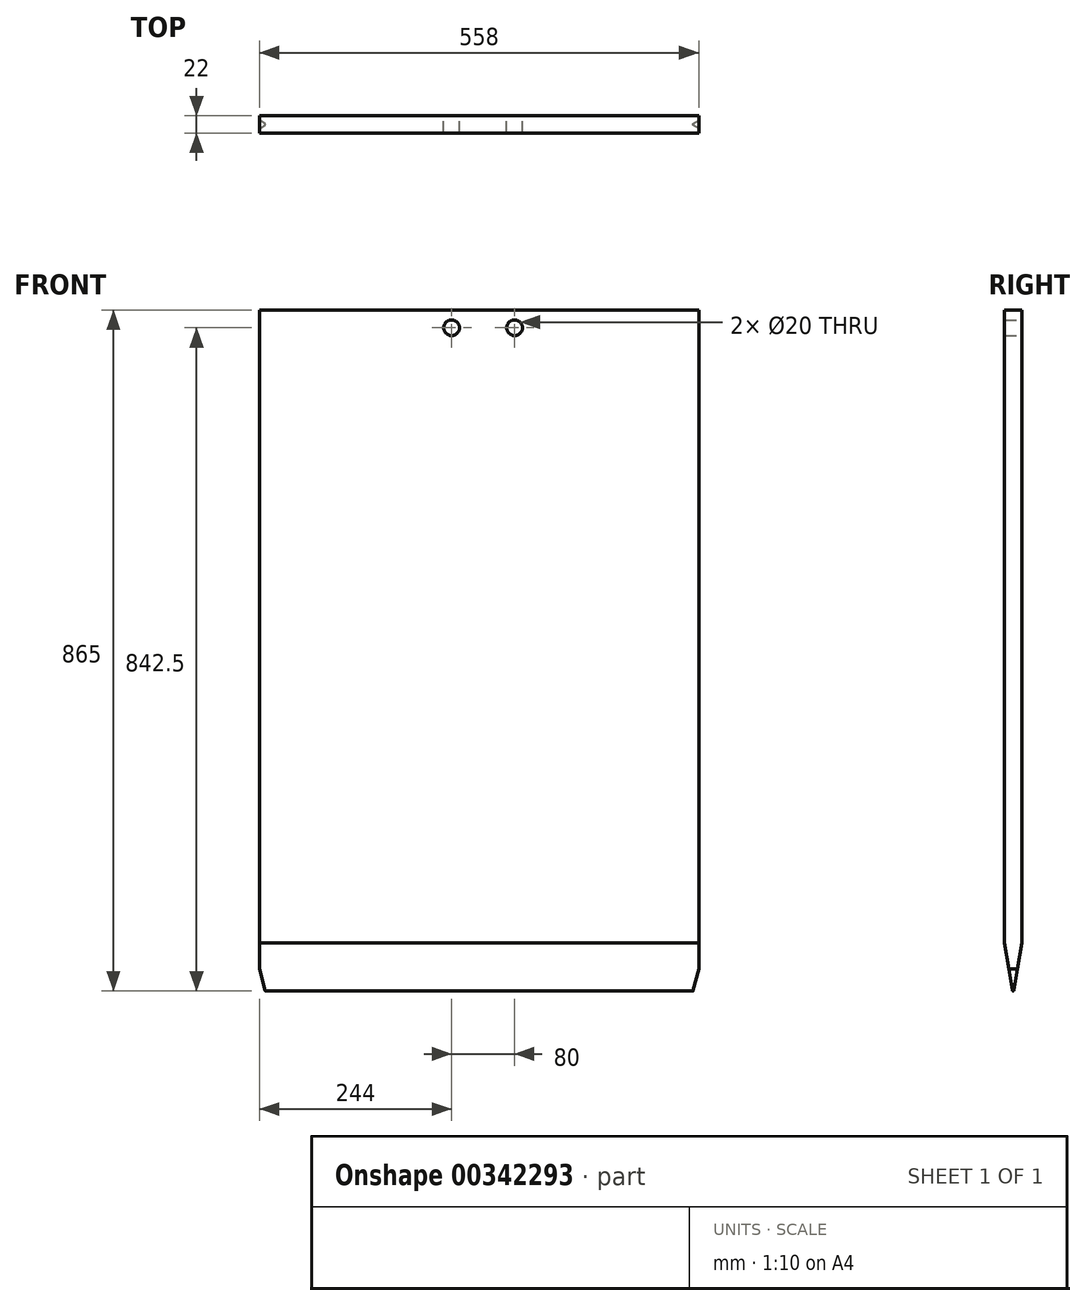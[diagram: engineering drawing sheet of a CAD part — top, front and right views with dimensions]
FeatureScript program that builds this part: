
annotation { "Feature Type Name" : "Feature", "Feature Type Description" : "" }
export const myFeature = defineFeature(function(context is Context, id is Id, definition is map)
    precondition{}
    {
        {
            var Q0;
            Q0=qCreatedBy(makeId("Right.planeOp"),FACE);
            var sketch = newSketch(context, id + "F0", { "sketchPlane" : qUnion([Q0])});
            skLineSegment(sketch, "E0.bottom", {"start": v(11, 432.5) * mm, "end": v(-11, 432.5) * mm});
            skLineSegment(sketch, "E0.top", {"start": v(11, -432.5) * mm, "end": v(-11, -432.5) * mm});
            skLineSegment(sketch, "E0.left", {"start": v(11, 432.5) * mm, "end": v(11, -432.5) * mm});
            skLineSegment(sketch, "E0.right", {"start": v(-11, 432.5) * mm, "end": v(-11, -432.5) * mm});
            skPoint(sketch, "E0.middle", {"position": v(0, 0) * mm});
            skPoint(sketch, "E1", {"position": v(0, -432.5) * mm});
            skCircle(sketch, "E2", {"center": v(0, -431.5) * mm, "radius": 1 * mm});
            skLineSegment(sketch, "E3", {"start": v(-11, -371.56) * mm, "end": v(-0.99, -431.66) * mm});
            skLineSegment(sketch, "E4", {"start": v(0.99, -431.66) * mm, "end": v(11, -371.56) * mm});
            skSolve(sketch);
        }
        {
            var Q0;
            {var subQ4=sQuery(id+"F0.wireOp",EDGE,"E0.bottom");Q0=makeQuery(id+"F0.imprint","IMPRINT",FACE,{"disambiguationData":[TD([[makeQuery(id+"F0.imprint","IMPRINT",EDGE,{"derivedFrom":subQ4}),1.0]])]});}
            var Q1;
            {var subQ0=sQuery(id+"F0.wireOp",EDGE,"E2");var subQ1=makeQuery(id+"F0.imprint","INTERSECT",VERTEX,{"derivedFrom":[subQ0,sQuery(id+"F0.wireOp",EDGE,"E3")]});Q1=makeQuery(id+"F0.imprint","IMPRINT",FACE,{"disambiguationData":[TD([[makeQuery(id+"F0.imprint","IMPRINT",EDGE,{"disambiguationData":[TD([[subQ1,-1.0]])],"derivedFrom":subQ0}),1.0]])]});}
            extrude(context, id + "F1", {"entities" : qUnion([Q0, Q1]), "endBound" : BoundingType.SYMMETRIC, "depth" : 558 * mm});
        }
        {
            var Q0;
            Q0=makeQuery(id+"F1.opExtrude","SWEPT_FACE",FACE,{"disambiguationData":[OSD([sQuery(id+"F0.wireOp",EDGE,"E0.left")])]});
            var sketch = newSketch(context, id + "F2", { "sketchPlane" : qUnion([Q0])});
            skCircle(sketch, "E5", {"center": v(-45, 410) * mm, "radius": 10 * mm});
            skCircle(sketch, "E6", {"center": v(35, 410) * mm, "radius": 10 * mm});
            skLineSegment(sketch, "E7", {"start": v(-279, -404.5) * mm, "end": v(-271.6, -432.5) * mm});
            skLineSegment(sketch, "E8", {"start": v(-279.1, -432.5) * mm, "end": v(-271.6, -432.5) * mm});
            skLineSegment(sketch, "E9", {"start": v(-279, -404.5) * mm, "end": v(-279.1, -432.5) * mm});
            skLineSegment(sketch, "E10.MirrorCS", {"start": v(279, -404.5) * mm, "end": v(271.6, -432.5) * mm});
            skLineSegment(sketch, "E11.MirrorCS", {"start": v(279, -404.5) * mm, "end": v(279.1, -432.5) * mm});
            skLineSegment(sketch, "E12.MirrorCS", {"start": v(279.1, -432.5) * mm, "end": v(271.6, -432.5) * mm});
            skSolve(sketch);
        }
        {
            var Q0;
            Q0 = qSketchRegion(id + "F2", true);
            extrude(context, id + "F3", {"entities" : qUnion([Q0]), "operationType" : NewBodyOperationType.REMOVE, "oppositeDirection" : true, "depth" : 25 * mm});
        }
    });
